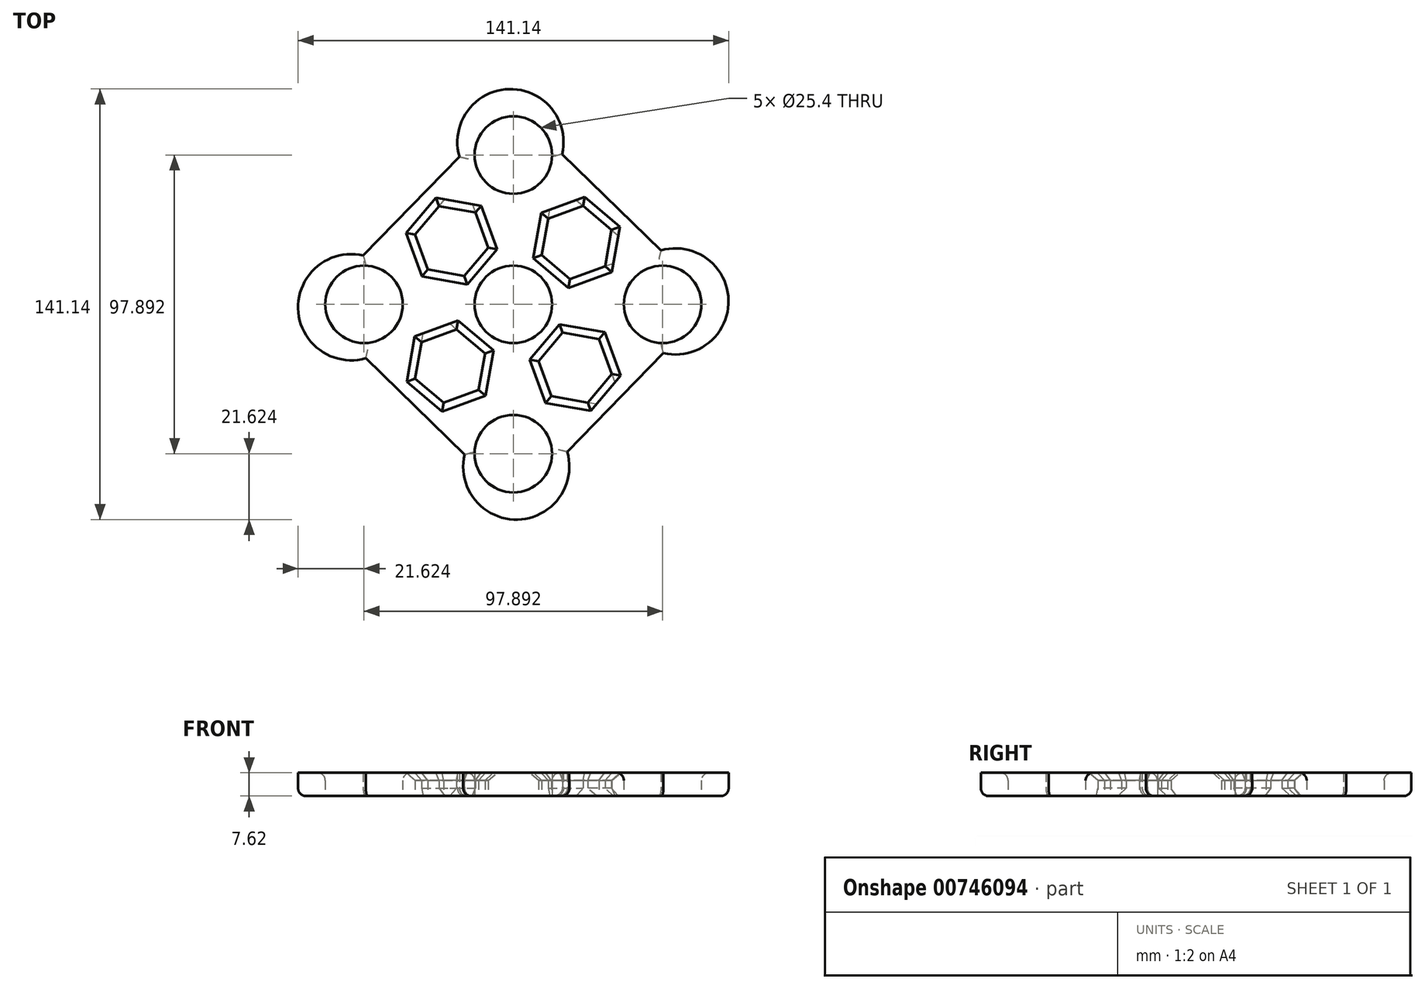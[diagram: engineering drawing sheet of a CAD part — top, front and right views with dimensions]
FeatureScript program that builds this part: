
annotation { "Feature Type Name" : "Feature", "Feature Type Description" : "" }
export const myFeature = defineFeature(function(context is Context, id is Id, definition is map)
    precondition{}
    {
        {
            var Q0;
            Q0=qCreatedBy(makeId("Top.planeOp"),FACE);
            var sketch = newSketch(context, id + "F0", { "sketchPlane" : qUnion([Q0])});
            skCircle(sketch, "E0", {"center": v(0, 0) * mm, "radius": 12.7 * mm});
            skCircle(sketch, "E1", {"center": v(0, 48.95) * mm, "radius": 12.7 * mm});
            skCircle(sketch, "E2.1.0", {"center": v(-48.95, 0) * mm, "radius": 12.7 * mm});
            skCircle(sketch, "E2.2.0", {"center": v(0, -48.95) * mm, "radius": 12.7 * mm});
            skCircle(sketch, "E2.3.0", {"center": v(48.95, 0) * mm, "radius": 12.7 * mm});
            skArc(sketch, "E3", {"start": v(16, 49.22) * mm, "mid": v(-1.4, 70.56) * mm, "end": v(-17.68, 48.37) * mm});
            skArc(sketch, "E4.1.0", {"start": v(-49.22, 16) * mm, "mid": v(-70.56, -1.4) * mm, "end": v(-48.37, -17.68) * mm});
            skArc(sketch, "E4.2.0", {"start": v(-16, -49.22) * mm, "mid": v(1.4, -70.56) * mm, "end": v(17.68, -48.37) * mm});
            skArc(sketch, "E4.3.0", {"start": v(49.22, -16) * mm, "mid": v(70.56, 1.4) * mm, "end": v(48.37, 17.68) * mm});
            skLineSegment(sketch, "E5", {"start": v(-49.22, 16) * mm, "end": v(-17.68, 48.37) * mm});
            skLineSegment(sketch, "E6.1.0", {"start": v(-16, -49.22) * mm, "end": v(-48.37, -17.68) * mm});
            skLineSegment(sketch, "E6.2.0", {"start": v(49.22, -16) * mm, "end": v(17.68, -48.37) * mm});
            skLineSegment(sketch, "E6.3.0", {"start": v(16, 49.22) * mm, "end": v(48.37, 17.68) * mm});
            skCircle(sketch, "E7.cCircle", {"center": v(-20.26, 20.74) * mm, "radius": 10.55 * mm, "construction": true});
            skLineSegment(sketch, "E7.0", {"start": v(-12.41, 30.06) * mm, "end": v(-8.26, 18.6) * mm});
            skLineSegment(sketch, "E7.1", {"start": v(-8.26, 18.6) * mm, "end": v(-16.11, 9.28) * mm});
            skLineSegment(sketch, "E7.2", {"start": v(-16.11, 9.28) * mm, "end": v(-28.11, 11.42) * mm});
            skLineSegment(sketch, "E7.3", {"start": v(-28.11, 11.42) * mm, "end": v(-32.26, 22.88) * mm});
            skLineSegment(sketch, "E7.4", {"start": v(-32.26, 22.88) * mm, "end": v(-24.4, 32.2) * mm});
            skLineSegment(sketch, "E7.5", {"start": v(-24.4, 32.2) * mm, "end": v(-12.41, 30.06) * mm});
            skPoint(sketch, "E7.0.midPoint", {"position": v(-10.34, 24.33) * mm});
            skPoint(sketch, "E8.1.0", {"position": v(-15.9, -21.12) * mm});
            skLineSegment(sketch, "E8.1.1", {"start": v(-11.98, -16.46) * mm, "end": v(0.02, -18.6) * mm});
            skLineSegment(sketch, "E8.1.2", {"start": v(-15.68, -37.24) * mm, "end": v(-19.83, -25.78) * mm});
            skLineSegment(sketch, "E8.1.3", {"start": v(0.02, -18.6) * mm, "end": v(4.16, -30.05) * mm});
            skPoint(sketch, "E8.2.0", {"position": v(26.24, -3.21) * mm});
            skLineSegment(sketch, "E8.2.1", {"start": v(20.24, -2.15) * mm, "end": v(16.1, 9.31) * mm});
            skLineSegment(sketch, "E8.2.2", {"start": v(40.09, 5.04) * mm, "end": v(32.24, -4.28) * mm});
            skLineSegment(sketch, "E8.2.3", {"start": v(16.1, 9.31) * mm, "end": v(23.95, 18.63) * mm});
            skLineSegment(sketch, "E9.1.0", {"start": v(-11.42, -28.11) * mm, "end": v(-22.88, -32.26) * mm});
            skLineSegment(sketch, "E9.1.1", {"start": v(-22.88, -32.26) * mm, "end": v(-32.2, -24.4) * mm});
            skLineSegment(sketch, "E9.1.2", {"start": v(-32.2, -24.4) * mm, "end": v(-30.06, -12.41) * mm});
            skPoint(sketch, "E9.1.3", {"position": v(-24.33, -10.34) * mm});
            skLineSegment(sketch, "E9.1.4", {"start": v(-30.06, -12.41) * mm, "end": v(-18.6, -8.26) * mm});
            skCircle(sketch, "E9.1.5", {"center": v(-20.74, -20.26) * mm, "radius": 10.55 * mm, "construction": true});
            skLineSegment(sketch, "E9.1.6", {"start": v(-9.28, -16.11) * mm, "end": v(-11.42, -28.11) * mm});
            skLineSegment(sketch, "E9.1.7", {"start": v(-18.6, -8.26) * mm, "end": v(-9.28, -16.11) * mm});
            skLineSegment(sketch, "E9.2.0", {"start": v(28.11, -11.42) * mm, "end": v(32.26, -22.88) * mm});
            skLineSegment(sketch, "E9.2.1", {"start": v(32.26, -22.88) * mm, "end": v(24.4, -32.2) * mm});
            skLineSegment(sketch, "E9.2.2", {"start": v(24.4, -32.2) * mm, "end": v(12.41, -30.06) * mm});
            skPoint(sketch, "E9.2.3", {"position": v(10.34, -24.33) * mm});
            skLineSegment(sketch, "E9.2.4", {"start": v(12.41, -30.06) * mm, "end": v(8.26, -18.6) * mm});
            skCircle(sketch, "E9.2.5", {"center": v(20.26, -20.74) * mm, "radius": 10.55 * mm, "construction": true});
            skLineSegment(sketch, "E9.2.6", {"start": v(16.11, -9.28) * mm, "end": v(28.11, -11.42) * mm});
            skLineSegment(sketch, "E9.2.7", {"start": v(8.26, -18.6) * mm, "end": v(16.11, -9.28) * mm});
            skLineSegment(sketch, "E9.3.0", {"start": v(11.42, 28.11) * mm, "end": v(22.88, 32.26) * mm});
            skLineSegment(sketch, "E9.3.1", {"start": v(22.88, 32.26) * mm, "end": v(32.2, 24.4) * mm});
            skLineSegment(sketch, "E9.3.2", {"start": v(32.2, 24.4) * mm, "end": v(30.06, 12.41) * mm});
            skPoint(sketch, "E9.3.3", {"position": v(24.33, 10.34) * mm});
            skLineSegment(sketch, "E9.3.4", {"start": v(30.06, 12.41) * mm, "end": v(18.6, 8.26) * mm});
            skCircle(sketch, "E9.3.5", {"center": v(20.74, 20.26) * mm, "radius": 10.55 * mm, "construction": true});
            skLineSegment(sketch, "E9.3.6", {"start": v(9.28, 16.11) * mm, "end": v(11.42, 28.11) * mm});
            skLineSegment(sketch, "E9.3.7", {"start": v(18.6, 8.26) * mm, "end": v(9.28, 16.11) * mm});
            skSolve(sketch);
        }
        {
            var Q0;
            Q0=makeQuery(id+"F0.imprint","IMPRINT",FACE,{"disambiguationData":[TD([[makeQuery(id+"F0.imprint","IMPRINT",EDGE,{"derivedFrom":sQuery(id+"F0.wireOp",EDGE,"E0")}),-1.0]])]});
            extrude(context, id + "F1", {"entities" : qUnion([Q0]), "depth" : 7.62 * mm, "offsetDistance" : 25.4 * mm});
        }
        {
            var Q0;
            Q0=makeQuery(id+"F1.opExtrude","CAP_EDGE",EDGE,{"disambiguationData":[OSD([sQuery(id+"F0.wireOp",EDGE,"E6.1.0")])],"isStart":true});
            var Q1;
            Q1=makeQuery(id+"F1.opExtrude","CAP_EDGE",EDGE,{"disambiguationData":[OSD([sQuery(id+"F0.wireOp",EDGE,"E4.1.0")])],"isStart":true});
            var Q2;
            Q2=makeQuery(id+"F1.opExtrude","CAP_EDGE",EDGE,{"disambiguationData":[OSD([sQuery(id+"F0.wireOp",EDGE,"E4.2.0")])],"isStart":true});
            var Q3;
            Q3=makeQuery(id+"F1.opExtrude","CAP_EDGE",EDGE,{"disambiguationData":[OSD([sQuery(id+"F0.wireOp",EDGE,"E5")])],"isStart":true});
            var Q4;
            Q4=makeQuery(id+"F1.opExtrude","CAP_EDGE",EDGE,{"disambiguationData":[OSD([sQuery(id+"F0.wireOp",EDGE,"E3")])],"isStart":true});
            var Q5;
            Q5=makeQuery(id+"F1.opExtrude","CAP_EDGE",EDGE,{"disambiguationData":[OSD([sQuery(id+"F0.wireOp",EDGE,"E6.3.0")])],"isStart":true});
            var Q6;
            Q6=makeQuery(id+"F1.opExtrude","CAP_EDGE",EDGE,{"disambiguationData":[OSD([sQuery(id+"F0.wireOp",EDGE,"E4.3.0")])],"isStart":true});
            var Q7;
            Q7=makeQuery(id+"F1.opExtrude","CAP_EDGE",EDGE,{"disambiguationData":[OSD([sQuery(id+"F0.wireOp",EDGE,"E6.2.0")])],"isStart":true});
            fillet(context, id + "F2", {"entities" : qUnion([Q0, Q1, Q2, Q3, Q4, Q5, Q6, Q7]), "radius" : 2.54 * mm, "tangentPropagation" : true, "allowEdgeOverflow" : false});
        }
        {
            var Q0;
            Q0=makeQuery(id+"F1.opExtrude","CAP_EDGE",EDGE,{"disambiguationData":[OSD([sQuery(id+"F0.wireOp",EDGE,"E7.5")])],"isStart":true});
            var Q1;
            Q1=makeQuery(id+"F1.opExtrude","CAP_EDGE",EDGE,{"disambiguationData":[OSD([sQuery(id+"F0.wireOp",EDGE,"E7.2")])],"isStart":false});
            var Q2;
            Q2=makeQuery(id+"F1.opExtrude","CAP_EDGE",EDGE,{"disambiguationData":[OSD([sQuery(id+"F0.wireOp",EDGE,"E7.3")])],"isStart":false});
            var Q3;
            Q3=makeQuery(id+"F1.opExtrude","CAP_EDGE",EDGE,{"disambiguationData":[OSD([sQuery(id+"F0.wireOp",EDGE,"E7.1")])],"isStart":false});
            var Q4;
            Q4=makeQuery(id+"F1.opExtrude","CAP_EDGE",EDGE,{"disambiguationData":[OSD([sQuery(id+"F0.wireOp",EDGE,"E7.5")])],"isStart":false});
            var Q5;
            Q5=makeQuery(id+"F1.opExtrude","CAP_EDGE",EDGE,{"disambiguationData":[OSD([sQuery(id+"F0.wireOp",EDGE,"E7.0")])],"isStart":false});
            var Q6;
            Q6=makeQuery(id+"F1.opExtrude","CAP_EDGE",EDGE,{"disambiguationData":[OSD([sQuery(id+"F0.wireOp",EDGE,"E9.3.0")])],"isStart":true});
            var Q7;
            Q7=makeQuery(id+"F1.opExtrude","CAP_EDGE",EDGE,{"disambiguationData":[OSD([sQuery(id+"F0.wireOp",EDGE,"E9.3.6")])],"isStart":false});
            var Q8;
            Q8=makeQuery(id+"F1.opExtrude","CAP_EDGE",EDGE,{"disambiguationData":[OSD([sQuery(id+"F0.wireOp",EDGE,"E9.3.7")])],"isStart":false});
            var Q9;
            Q9=makeQuery(id+"F1.opExtrude","CAP_EDGE",EDGE,{"disambiguationData":[OSD([sQuery(id+"F0.wireOp",EDGE,"E9.3.4")])],"isStart":false});
            var Q10;
            Q10=makeQuery(id+"F1.opExtrude","CAP_EDGE",EDGE,{"disambiguationData":[OSD([sQuery(id+"F0.wireOp",EDGE,"E9.3.2")])],"isStart":true});
            var Q11;
            Q11=makeQuery(id+"F1.opExtrude","CAP_EDGE",EDGE,{"disambiguationData":[OSD([sQuery(id+"F0.wireOp",EDGE,"E9.3.1")])],"isStart":false});
            var Q12;
            Q12=makeQuery(id+"F1.opExtrude","CAP_EDGE",EDGE,{"disambiguationData":[OSD([sQuery(id+"F0.wireOp",EDGE,"E9.3.2")])],"isStart":false});
            var Q13;
            Q13=makeQuery(id+"F1.opExtrude","CAP_EDGE",EDGE,{"disambiguationData":[OSD([sQuery(id+"F0.wireOp",EDGE,"E9.3.0")])],"isStart":false});
            var Q14;
            Q14=makeQuery(id+"F1.opExtrude","CAP_EDGE",EDGE,{"disambiguationData":[OSD([sQuery(id+"F0.wireOp",EDGE,"E9.2.6")])],"isStart":false});
            var Q15;
            Q15=makeQuery(id+"F1.opExtrude","CAP_EDGE",EDGE,{"disambiguationData":[OSD([sQuery(id+"F0.wireOp",EDGE,"E9.2.0")])],"isStart":false});
            var Q16;
            Q16=makeQuery(id+"F1.opExtrude","CAP_EDGE",EDGE,{"disambiguationData":[OSD([sQuery(id+"F0.wireOp",EDGE,"E9.2.1")])],"isStart":true});
            var Q17;
            Q17=makeQuery(id+"F1.opExtrude","CAP_EDGE",EDGE,{"disambiguationData":[OSD([sQuery(id+"F0.wireOp",EDGE,"E9.2.1")])],"isStart":false});
            var Q18;
            Q18=makeQuery(id+"F1.opExtrude","CAP_EDGE",EDGE,{"disambiguationData":[OSD([sQuery(id+"F0.wireOp",EDGE,"E9.2.2")])],"isStart":false});
            var Q19;
            Q19=makeQuery(id+"F1.opExtrude","CAP_EDGE",EDGE,{"disambiguationData":[OSD([sQuery(id+"F0.wireOp",EDGE,"E9.2.4")])],"isStart":false});
            var Q20;
            Q20=makeQuery(id+"F1.opExtrude","CAP_EDGE",EDGE,{"disambiguationData":[OSD([sQuery(id+"F0.wireOp",EDGE,"E9.2.7")])],"isStart":false});
            var Q21;
            Q21=makeQuery(id+"F1.opExtrude","CAP_EDGE",EDGE,{"disambiguationData":[OSD([sQuery(id+"F0.wireOp",EDGE,"E9.1.4")])],"isStart":true});
            var Q22;
            Q22=makeQuery(id+"F1.opExtrude","CAP_EDGE",EDGE,{"disambiguationData":[OSD([sQuery(id+"F0.wireOp",EDGE,"E9.1.4")])],"isStart":false});
            var Q23;
            Q23=makeQuery(id+"F1.opExtrude","CAP_EDGE",EDGE,{"disambiguationData":[OSD([sQuery(id+"F0.wireOp",EDGE,"E9.1.6")])],"isStart":false});
            var Q24;
            Q24=makeQuery(id+"F1.opExtrude","CAP_EDGE",EDGE,{"disambiguationData":[OSD([sQuery(id+"F0.wireOp",EDGE,"E9.1.7")])],"isStart":false});
            var Q25;
            Q25=makeQuery(id+"F1.opExtrude","CAP_EDGE",EDGE,{"disambiguationData":[OSD([sQuery(id+"F0.wireOp",EDGE,"E9.1.0")])],"isStart":false});
            var Q26;
            Q26=makeQuery(id+"F1.opExtrude","CAP_EDGE",EDGE,{"disambiguationData":[OSD([sQuery(id+"F0.wireOp",EDGE,"E9.1.1")])],"isStart":false});
            var Q27;
            Q27=makeQuery(id+"F1.opExtrude","CAP_EDGE",EDGE,{"disambiguationData":[OSD([sQuery(id+"F0.wireOp",EDGE,"E9.1.2")])],"isStart":false});
            var Q28;
            Q28=makeQuery(id+"F1.opExtrude","CAP_EDGE",EDGE,{"disambiguationData":[OSD([sQuery(id+"F0.wireOp",EDGE,"E7.4")])],"isStart":false});
            chamfer(context, id + "F3", {"entities" : qUnion([Q0, Q1, Q2, Q3, Q4, Q5, Q6, Q7, Q8, Q9, Q10, Q11, Q12, Q13, Q14, Q15, Q16, Q17, Q18, Q19, Q20, Q21, Q22, Q23, Q24, Q25, Q26, Q27, Q28]), "width" : 2.54 * mm, "tangentPropagation" : true});
        }
        {
            var Q0;
            Q0=makeQuery(id+"F1.opExtrude","CAP_EDGE",EDGE,{"disambiguationData":[OSD([sQuery(id+"F0.wireOp",EDGE,"E2.1.0")])],"isStart":false});
            var Q1;
            Q1=makeQuery(id+"F1.opExtrude","CAP_EDGE",EDGE,{"disambiguationData":[OSD([sQuery(id+"F0.wireOp",EDGE,"E2.2.0")])],"isStart":false});
            var Q2;
            Q2=makeQuery(id+"F1.opExtrude","CAP_EDGE",EDGE,{"disambiguationData":[OSD([sQuery(id+"F0.wireOp",EDGE,"E1")])],"isStart":false});
            var Q3;
            Q3=makeQuery(id+"F1.opExtrude","CAP_EDGE",EDGE,{"disambiguationData":[OSD([sQuery(id+"F0.wireOp",EDGE,"E2.3.0")])],"isStart":false});
            fillet(context, id + "F4", {"entities" : qUnion([Q0, Q1, Q2, Q3]), "radius" : 2.54 * mm, "tangentPropagation" : true, "allowEdgeOverflow" : false});
        }
    });
